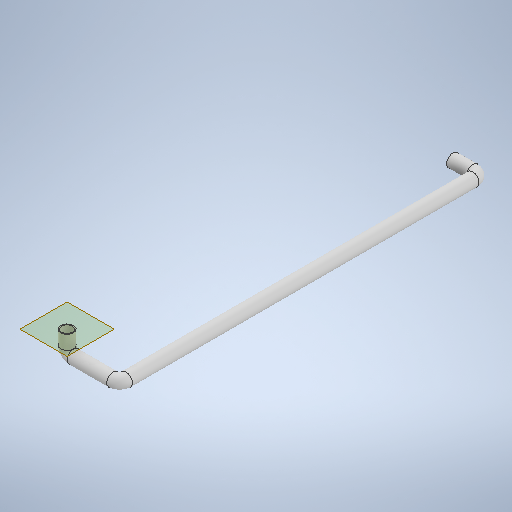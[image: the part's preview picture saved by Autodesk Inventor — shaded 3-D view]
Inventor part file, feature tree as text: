
AUTODESK INVENTOR PART (.ipt)
format: ipt  version: 2025.2 (Build 292293000, 293)  size: 275,456 bytes
history: native  units: mm
features: sketch x2, plane x1, sweep x1
ambient origin geometry x8: Origin, YZ Plane, XZ Plane, XY Plane, X Axis, Y Axis, Z Axis, Center Point
bodies: Solid1 (feature_tree)
feature tree (4):
  sketch  "3D Sketch1"
  plane  "Work Plane1"
  sweep  "Sweep1"
  sketch  "Sketch1"  dims[d0=6.497mm d1=3.0mm d2=90.0deg d3=18.5mm d4=90.0deg d5=161.75mm d6=90.0deg d7=9.25mm d8=6.0mm d9=5.0mm d10=0.0mm d11=0.0mm]
